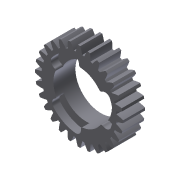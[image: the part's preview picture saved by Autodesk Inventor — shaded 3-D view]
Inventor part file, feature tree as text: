
AUTODESK INVENTOR PART (.ipt)
format: ipt  version: 2013 (Build 170138000, 138)  size: 312,320 bytes
history: native  units: mm (DEFAULTED — no unit token found)
features: sketch x4, plane x3, other x3, extrude x2, hole x1, fillet x1, pattern_circular x1
ambient origin geometry x8: Origin, YZ Plane, XZ Plane, XY Plane, X Axis, Y Axis, Z Axis, Center Point
bodies: Solid1 (feature_tree)
feature tree (15):
  extrude  "Extrusion1"  Depth=9.525mm TaperAngle=0.0deg
  plane  "Work Plane1"
  plane  "Work Plane2"
  plane  "Work Plane3"
  other  "Spur Gear"
  hole  "Hole1"  [1 undecoded]
  extrude  "Extrusion4"  TaperAngle=0.0deg  [1 undecoded]
  fillet  "Fillet1"  Radius=11.170107mm
  pattern_circular  "Circular Pattern1"  [2 undecoded]
  sketch  "Sketch1"  dims[d0=38.2016mm d1=9.525mm d2=0.0mm]
  sketch  "Sketch2"  dims[d3=35.56mm d4=76.2mm d5=0.0mm]
  other  "Srf1"
  sketch  "Sketch6"  dims[d6=0.0mm d7=1.121997mm d9=0.0mm]
  sketch  "Sketch7"  dims[d32=22.1996mm d33=19.05mm d34=9.525mm d35=6.35mm d36=14.3117mm d37=25.4mm d38=20.594885mm d39=11.170107mm d40=1.6002mm d41=2.286mm d42=3.175mm d43=0.0mm d44=0.762mm d45=30.0mm d46=360.0deg]
  other  "Pitch Diameter"
note: 4 required parameter values undecoded (feature->parameter linkage not recoverable at this tier; creation-order binding heuristic only, values carry confidence <= 0.55)
